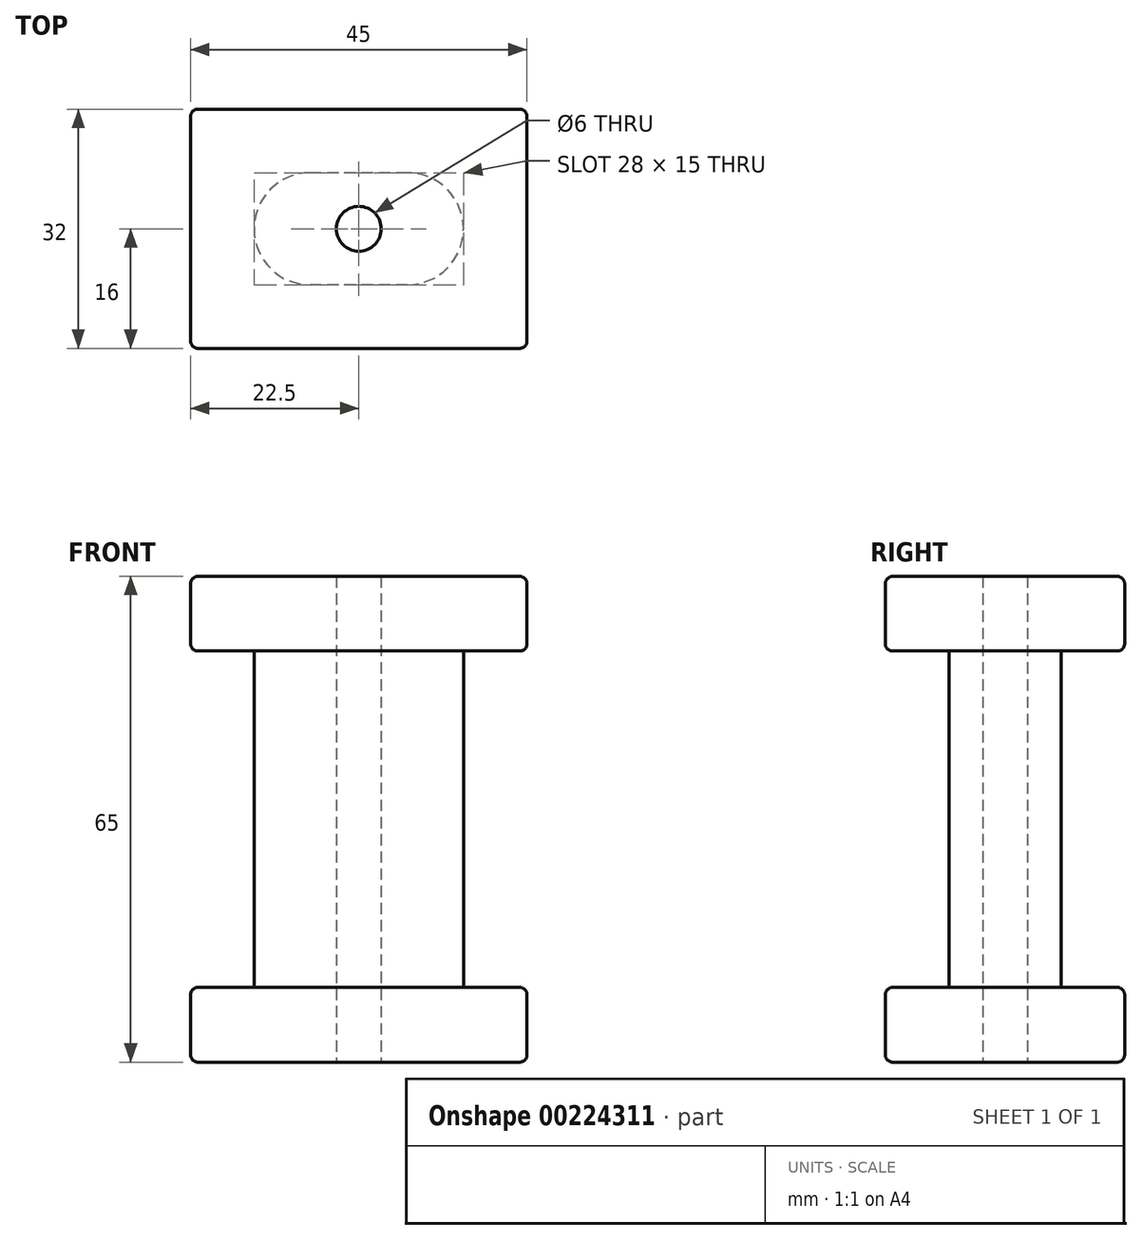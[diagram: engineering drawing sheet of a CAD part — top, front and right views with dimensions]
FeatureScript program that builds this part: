
annotation { "Feature Type Name" : "Feature", "Feature Type Description" : "" }
export const myFeature = defineFeature(function(context is Context, id is Id, definition is map)
    precondition{}
    {
        {
            var Q0;
            Q0=qCreatedBy(makeId("Top.planeOp"),FACE);
            var sketch = newSketch(context, id + "F0", { "sketchPlane" : qUnion([Q0])});
            skLineSegment(sketch, "E0.bottom", {"start": v(6.5, 7.5) * mm, "end": v(-6.5, 7.5) * mm});
            skLineSegment(sketch, "E0.top", {"start": v(6.5, -7.5) * mm, "end": v(-6.5, -7.5) * mm});
            skPoint(sketch, "E0.middle", {"position": v(0, 0) * mm});
            skLineSegment(sketch, "E1.bottom", {"start": v(22.5, 16) * mm, "end": v(-22.5, 16) * mm});
            skLineSegment(sketch, "E1.top", {"start": v(22.5, -16) * mm, "end": v(-22.5, -16) * mm});
            skLineSegment(sketch, "E1.left", {"start": v(22.5, 16) * mm, "end": v(22.5, -16) * mm});
            skLineSegment(sketch, "E1.right", {"start": v(-22.5, 16) * mm, "end": v(-22.5, -16) * mm});
            skCircle(sketch, "E2", {"center": v(0, 0) * mm, "radius": 3 * mm});
            skArc(sketch, "E3", {"start": v(-6.5, 7.5) * mm, "mid": v(-14, 0) * mm, "end": v(-6.5, -7.5) * mm});
            skArc(sketch, "E4.trimOffspring", {"start": v(6.5, -7.5) * mm, "mid": v(14, 0) * mm, "end": v(6.5, 7.5) * mm});
            skSolve(sketch);
        }
        {
            var Q0;
            Q0=makeQuery(id+"F0.imprint","IMPRINT",FACE,{"disambiguationData":[TD([[makeQuery(id+"F0.imprint","IMPRINT",EDGE,{"derivedFrom":sQuery(id+"F0.wireOp",EDGE,"E0.bottom")}),1.0]])]});
            extrude(context, id + "F1", {"entities" : qUnion([Q0]), "endBound" : BoundingType.SYMMETRIC, "depth" : 45 * mm});
        }
        {
            var Q0;
            Q0=makeQuery(id+"F0.imprint","IMPRINT",FACE,{"disambiguationData":[TD([[makeQuery(id+"F0.imprint","IMPRINT",EDGE,{"derivedFrom":sQuery(id+"F0.wireOp",EDGE,"E0.bottom")}),-1.0]])]});
            cPlane(context, id + "F2", {"entities" : qUnion([Q0]), "cplaneType" : CPlaneType.OFFSET, "offset" : 22.5 * mm, "width" : 150 * mm, "height" : 150 * mm});
        }
        {
            var Q0;
            Q0=makeQuery(id+"F0.imprint","IMPRINT",FACE,{"disambiguationData":[TD([[makeQuery(id+"F0.imprint","IMPRINT",EDGE,{"derivedFrom":sQuery(id+"F0.wireOp",EDGE,"E0.bottom")}),-1.0]])]});
            cPlane(context, id + "F3", {"entities" : qUnion([Q0]), "cplaneType" : CPlaneType.OFFSET, "offset" : 22.5 * mm, "oppositeDirection" : true, "width" : 150 * mm, "height" : 150 * mm});
        }
        {
            var Q0;
            Q0=qCreatedBy(id+"F2.planeOp",FACE);
            var sketch = newSketch(context, id + "F4", { "sketchPlane" : qUnion([Q0])});
            skLineSegment(sketch, "E5.bottom", {"start": v(-22.5, 16) * mm, "end": v(22.5, 16) * mm});
            skLineSegment(sketch, "E5.top", {"start": v(-22.5, -16) * mm, "end": v(22.5, -16) * mm});
            skLineSegment(sketch, "E5.left", {"start": v(-22.5, 16) * mm, "end": v(-22.5, -16) * mm});
            skLineSegment(sketch, "E5.right", {"start": v(22.5, 16) * mm, "end": v(22.5, -16) * mm});
            skPoint(sketch, "E5.middle", {"position": v(0, 0) * mm});
            skCircle(sketch, "E6", {"center": v(0, 0) * mm, "radius": 3 * mm});
            skSolve(sketch);
        }
        {
            var Q0;
            Q0=makeQuery(id+"F4.imprint","IMPRINT",FACE,{"disambiguationData":[TD([[makeQuery(id+"F4.imprint","IMPRINT",EDGE,{"derivedFrom":sQuery(id+"F4.wireOp",EDGE,"E5.bottom")}),-1.0]])]});
            extrude(context, id + "F5", {"entities" : qUnion([Q0]), "operationType" : NewBodyOperationType.ADD, "depth" : 10 * mm});
        }
        {
            var Q0;
            Q0=qCreatedBy(id+"F3.planeOp",FACE);
            var sketch = newSketch(context, id + "F6", { "sketchPlane" : qUnion([Q0])});
            skLineSegment(sketch, "E7.bottom", {"start": v(22.5, -16) * mm, "end": v(-22.5, -16) * mm});
            skLineSegment(sketch, "E7.top", {"start": v(22.5, 16) * mm, "end": v(-22.5, 16) * mm});
            skLineSegment(sketch, "E7.left", {"start": v(22.5, -16) * mm, "end": v(22.5, 16) * mm});
            skLineSegment(sketch, "E7.right", {"start": v(-22.5, -16) * mm, "end": v(-22.5, 16) * mm});
            skPoint(sketch, "E7.middle", {"position": v(0, 0) * mm});
            skCircle(sketch, "E8", {"center": v(0, 0) * mm, "radius": 3 * mm});
            skSolve(sketch);
        }
        {
            var Q0;
            Q0=makeQuery(id+"F6.imprint","IMPRINT",FACE,{"disambiguationData":[TD([[makeQuery(id+"F6.imprint","IMPRINT",EDGE,{"derivedFrom":sQuery(id+"F6.wireOp",EDGE,"E7.bottom")}),-1.0]])]});
            extrude(context, id + "F7", {"entities" : qUnion([Q0]), "operationType" : NewBodyOperationType.ADD, "oppositeDirection" : true, "depth" : 10 * mm});
        }
        {
            var Q0;
            Q0=makeQuery(id+"F7.opExtrude","CAP_EDGE",EDGE,{"disambiguationData":[OSD([sQuery(id+"F6.wireOp",EDGE,"E7.top")])],"isStart":false});
            var Q1;
            Q1=makeQuery(id+"F7.opExtrude","CAP_EDGE",EDGE,{"disambiguationData":[OSD([sQuery(id+"F6.wireOp",EDGE,"E7.left")])],"isStart":false});
            var Q2;
            Q2=makeQuery(id+"F7.opExtrude","CAP_EDGE",EDGE,{"disambiguationData":[OSD([sQuery(id+"F6.wireOp",EDGE,"E7.bottom")])],"isStart":false});
            var Q3;
            Q3=makeQuery(id+"F7.opExtrude","CAP_EDGE",EDGE,{"disambiguationData":[OSD([sQuery(id+"F6.wireOp",EDGE,"E7.right")])],"isStart":false});
            var Q4;
            Q4=makeQuery(id+"F7.opExtrude","CAP_EDGE",EDGE,{"disambiguationData":[OSD([sQuery(id+"F6.wireOp",EDGE,"E7.top")])],"isStart":true});
            var Q5;
            Q5=makeQuery(id+"F7.opExtrude","SWEPT_EDGE",EDGE,{"disambiguationData":[OSD([sQuery(id+"F6.wireOp",EDGE,"E7.top"),sQuery(id+"F6.wireOp",EDGE,"E7.left")])]});
            var Q6;
            Q6=makeQuery(id+"F7.opExtrude","CAP_EDGE",EDGE,{"disambiguationData":[OSD([sQuery(id+"F6.wireOp",EDGE,"E7.left")])],"isStart":true});
            var Q7;
            Q7=makeQuery(id+"F7.opExtrude","SWEPT_EDGE",EDGE,{"disambiguationData":[OSD([sQuery(id+"F6.wireOp",EDGE,"E7.bottom"),sQuery(id+"F6.wireOp",EDGE,"E7.left")])]});
            var Q8;
            Q8=makeQuery(id+"F7.opExtrude","CAP_EDGE",EDGE,{"disambiguationData":[OSD([sQuery(id+"F6.wireOp",EDGE,"E7.bottom")])],"isStart":true});
            var Q9;
            Q9=makeQuery(id+"F7.opExtrude","SWEPT_EDGE",EDGE,{"disambiguationData":[OSD([sQuery(id+"F6.wireOp",EDGE,"E7.bottom"),sQuery(id+"F6.wireOp",EDGE,"E7.right")])]});
            var Q10;
            Q10=makeQuery(id+"F7.opExtrude","CAP_EDGE",EDGE,{"disambiguationData":[OSD([sQuery(id+"F6.wireOp",EDGE,"E7.right")])],"isStart":true});
            var Q11;
            Q11=makeQuery(id+"F7.opExtrude","SWEPT_EDGE",EDGE,{"disambiguationData":[OSD([sQuery(id+"F6.wireOp",EDGE,"E7.top"),sQuery(id+"F6.wireOp",EDGE,"E7.right")])]});
            var Q12;
            Q12=makeQuery(id+"F1.opExtrude","CAP_EDGE",EDGE,{"disambiguationData":[OSD([sQuery(id+"F0.wireOp",EDGE,"E0.bottom")])],"isStart":true});
            var Q13;
            Q13=makeQuery(id+"F1.opExtrude","CAP_EDGE",EDGE,{"disambiguationData":[OSD([sQuery(id+"F0.wireOp",EDGE,"E3")])],"isStart":false});
            var Q14;
            Q14=makeQuery(id+"F5.opExtrude","SWEPT_EDGE",EDGE,{"disambiguationData":[OSD([sQuery(id+"F4.wireOp",EDGE,"E5.bottom"),sQuery(id+"F4.wireOp",EDGE,"E5.left")])]});
            var Q15;
            Q15=makeQuery(id+"F5.opExtrude","CAP_EDGE",EDGE,{"disambiguationData":[OSD([sQuery(id+"F4.wireOp",EDGE,"E5.left")])],"isStart":true});
            var Q16;
            Q16=makeQuery(id+"F5.opExtrude","CAP_EDGE",EDGE,{"disambiguationData":[OSD([sQuery(id+"F4.wireOp",EDGE,"E5.bottom")])],"isStart":true});
            var Q17;
            Q17=makeQuery(id+"F5.opExtrude","CAP_EDGE",EDGE,{"disambiguationData":[OSD([sQuery(id+"F4.wireOp",EDGE,"E5.left")])],"isStart":false});
            var Q18;
            Q18=makeQuery(id+"F5.opExtrude","CAP_EDGE",EDGE,{"disambiguationData":[OSD([sQuery(id+"F4.wireOp",EDGE,"E5.bottom")])],"isStart":false});
            var Q19;
            Q19=makeQuery(id+"F5.opExtrude","SWEPT_EDGE",EDGE,{"disambiguationData":[OSD([sQuery(id+"F4.wireOp",EDGE,"E5.top"),sQuery(id+"F4.wireOp",EDGE,"E5.left")])]});
            var Q20;
            Q20=makeQuery(id+"F5.opExtrude","CAP_EDGE",EDGE,{"disambiguationData":[OSD([sQuery(id+"F4.wireOp",EDGE,"E5.top")])],"isStart":false});
            var Q21;
            Q21=makeQuery(id+"F5.opExtrude","CAP_EDGE",EDGE,{"disambiguationData":[OSD([sQuery(id+"F4.wireOp",EDGE,"E5.top")])],"isStart":true});
            var Q22;
            Q22=makeQuery(id+"F5.opExtrude","SWEPT_EDGE",EDGE,{"disambiguationData":[OSD([sQuery(id+"F4.wireOp",EDGE,"E5.top"),sQuery(id+"F4.wireOp",EDGE,"E5.right")])]});
            var Q23;
            Q23=makeQuery(id+"F5.opExtrude","CAP_EDGE",EDGE,{"disambiguationData":[OSD([sQuery(id+"F4.wireOp",EDGE,"E5.right")])],"isStart":true});
            var Q24;
            Q24=makeQuery(id+"F5.opExtrude","CAP_EDGE",EDGE,{"disambiguationData":[OSD([sQuery(id+"F4.wireOp",EDGE,"E5.right")])],"isStart":false});
            var Q25;
            Q25=makeQuery(id+"F5.opExtrude","SWEPT_EDGE",EDGE,{"disambiguationData":[OSD([sQuery(id+"F4.wireOp",EDGE,"E5.bottom"),sQuery(id+"F4.wireOp",EDGE,"E5.right")])]});
            fillet(context, id + "F8", {"entities" : qUnion([Q0, Q1, Q2, Q3, Q4, Q5, Q6, Q7, Q8, Q9, Q10, Q11, Q12, Q13, Q14, Q15, Q16, Q17, Q18, Q19, Q20, Q21, Q22, Q23, Q24, Q25]), "radius" : 1 * mm, "tangentPropagation" : true, "allowEdgeOverflow" : false});
        }
    });
